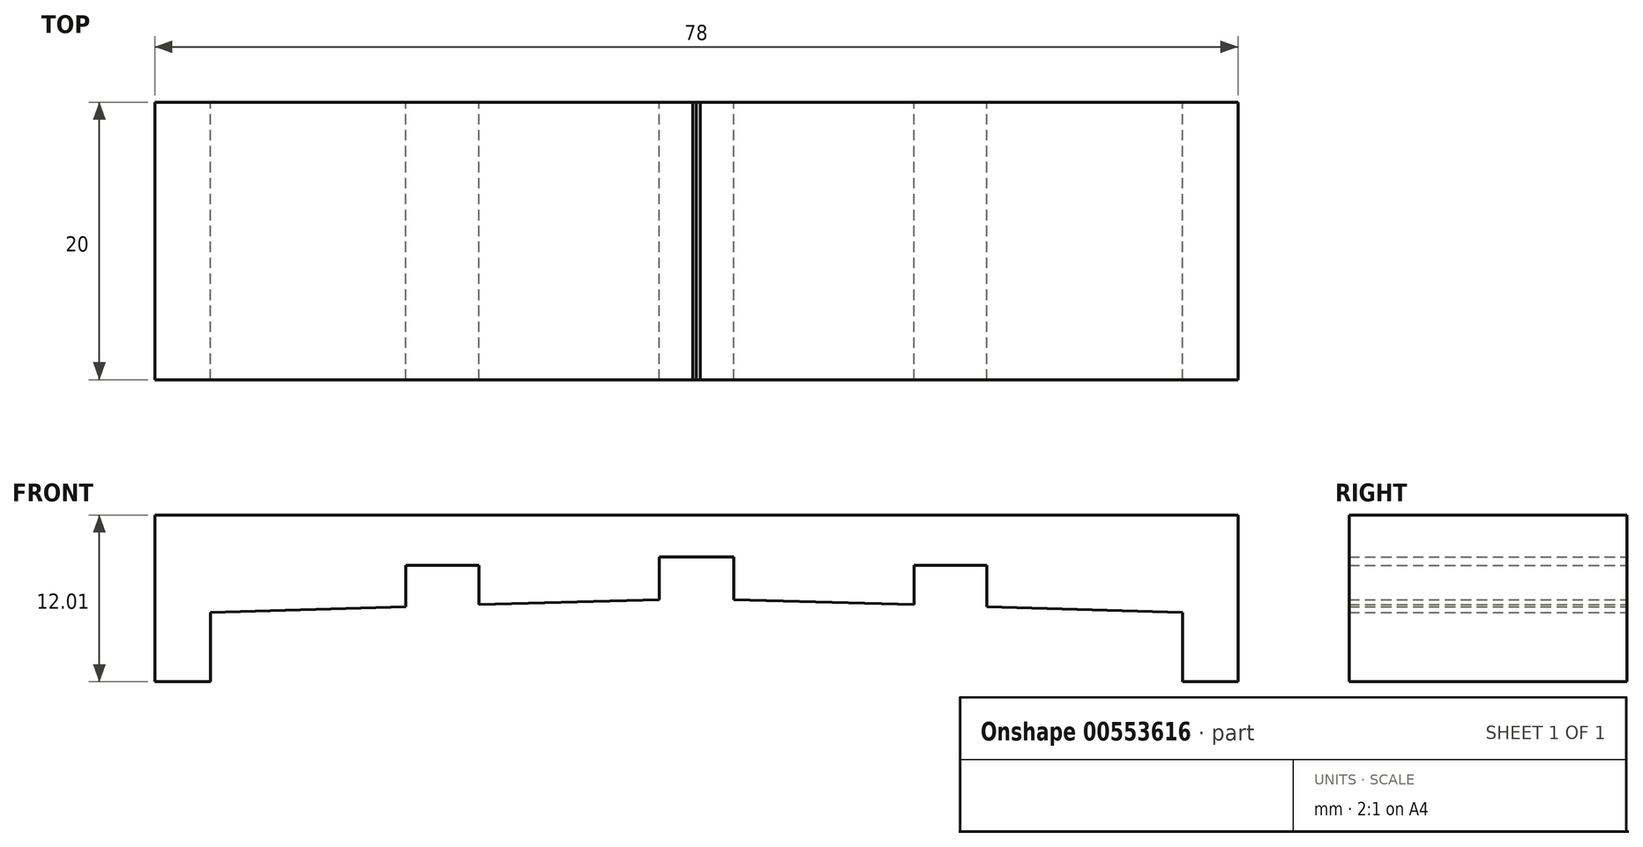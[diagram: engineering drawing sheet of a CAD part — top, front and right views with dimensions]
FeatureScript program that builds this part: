
annotation { "Feature Type Name" : "Feature", "Feature Type Description" : "" }
export const myFeature = defineFeature(function(context is Context, id is Id, definition is map)
    precondition{}
    {
        {
            var Q0;
            Q0=qCreatedBy(makeId("Front.planeOp"),FACE);
            var sketch = newSketch(context, id + "F0", { "sketchPlane" : qUnion([Q0])});
            skLineSegment(sketch, "E0", {"start": v(-28.86, 0) * mm, "end": v(26.04, 0) * mm, "construction": true});
            skLineSegment(sketch, "E1", {"start": v(0, 15.37) * mm, "end": v(0, -13.35) * mm, "construction": true});
            skLineSegment(sketch, "E2", {"start": v(-2.67, -0.08) * mm, "end": v(-2.67, 3) * mm});
            skLineSegment(sketch, "E3", {"start": v(-2.67, 3) * mm, "end": v(0, 3) * mm});
            skLineSegment(sketch, "E4", {"start": v(0, 3) * mm, "end": v(0, 3) * mm});
            skLineSegment(sketch, "E5", {"start": v(-2.67, -0.08) * mm, "end": v(-15.68, -0.45) * mm});
            skLineSegment(sketch, "E6", {"start": v(-35, -1) * mm, "end": v(-35, -6) * mm});
            skLineSegment(sketch, "E7", {"start": v(-35, -6) * mm, "end": v(-39, -6) * mm});
            skLineSegment(sketch, "E8", {"start": v(-39, -6) * mm, "end": v(-39, 4.82) * mm});
            skPoint(sketch, "E9", {"position": v(-20.93, 2.4) * mm});
            skPoint(sketch, "E10", {"position": v(-20.93, -0.6) * mm});
            skLineSegment(sketch, "E11.trimOffspring", {"start": v(-20.93, -0.6) * mm, "end": v(-35, -1) * mm});
            skLineSegment(sketch, "E12", {"start": v(-20.93, -0.6) * mm, "end": v(-20.93, 2.4) * mm});
            skLineSegment(sketch, "E13", {"start": v(-20.93, 2.4) * mm, "end": v(-15.68, 2.4) * mm});
            skLineSegment(sketch, "E14", {"start": v(-15.68, 2.4) * mm, "end": v(-15.68, -0.45) * mm});
            skPoint(sketch, "E15", {"position": v(-2.67, -0.08) * mm});
            skPoint(sketch, "E16.orphan", {"position": v(0, 0) * mm});
            skLineSegment(sketch, "E17", {"start": v(-0.26, 6) * mm, "end": v(0, 6) * mm});
            skLineSegment(sketch, "E18.MirrorCS", {"start": v(0.26, 6) * mm, "end": v(0, 6) * mm});
            skPoint(sketch, "E19.MirrorP", {"position": v(20.93, 2.4) * mm});
            skLineSegment(sketch, "E20.MirrorCS", {"start": v(20.93, -0.6) * mm, "end": v(35, -1) * mm});
            skLineSegment(sketch, "E21.MirrorCS", {"start": v(20.93, 2.4) * mm, "end": v(15.68, 2.4) * mm});
            skLineSegment(sketch, "E22.MirrorCS", {"start": v(15.68, 2.4) * mm, "end": v(15.68, -0.45) * mm});
            skLineSegment(sketch, "E23.MirrorCS", {"start": v(2.68, 3) * mm, "end": v(0, 3) * mm});
            skLineSegment(sketch, "E24.MirrorCS", {"start": v(2.68, -0.08) * mm, "end": v(2.68, 3) * mm});
            skLineSegment(sketch, "E25.MirrorCS", {"start": v(35, -1) * mm, "end": v(35, -6) * mm});
            skPoint(sketch, "E26.MirrorP", {"position": v(20.93, -0.6) * mm});
            skLineSegment(sketch, "E27.MirrorCS", {"start": v(28.86, 0) * mm, "end": v(-26.04, 0) * mm, "construction": true});
            skLineSegment(sketch, "E28.MirrorCS", {"start": v(20.93, -0.6) * mm, "end": v(20.93, 2.4) * mm});
            skLineSegment(sketch, "E29.MirrorCS", {"start": v(35, -6) * mm, "end": v(39, -6) * mm});
            skLineSegment(sketch, "E30.MirrorCS", {"start": v(2.67, -0.08) * mm, "end": v(15.68, -0.45) * mm});
            skLineSegment(sketch, "E31.MirrorCS", {"start": v(39, -6) * mm, "end": v(39, 4.82) * mm});
            skPoint(sketch, "E32.MirrorP", {"position": v(2.68, -0.08) * mm});
            skLineSegment(sketch, "E33", {"start": v(-39, 6) * mm, "end": v(39, 6) * mm});
            skLineSegment(sketch, "E34", {"start": v(39, 6) * mm, "end": v(39, 4.82) * mm});
            skLineSegment(sketch, "E35", {"start": v(-39, 6) * mm, "end": v(-39, 4.82) * mm});
            skSolve(sketch);
        }
        {
            var Q0;
            Q0 = qSketchRegion(id + "F0", true);
            extrude(context, id + "F1", {"entities" : qUnion([Q0]), "depth" : 20 * mm, "offsetDistance" : 25 * mm});
        }
    });
